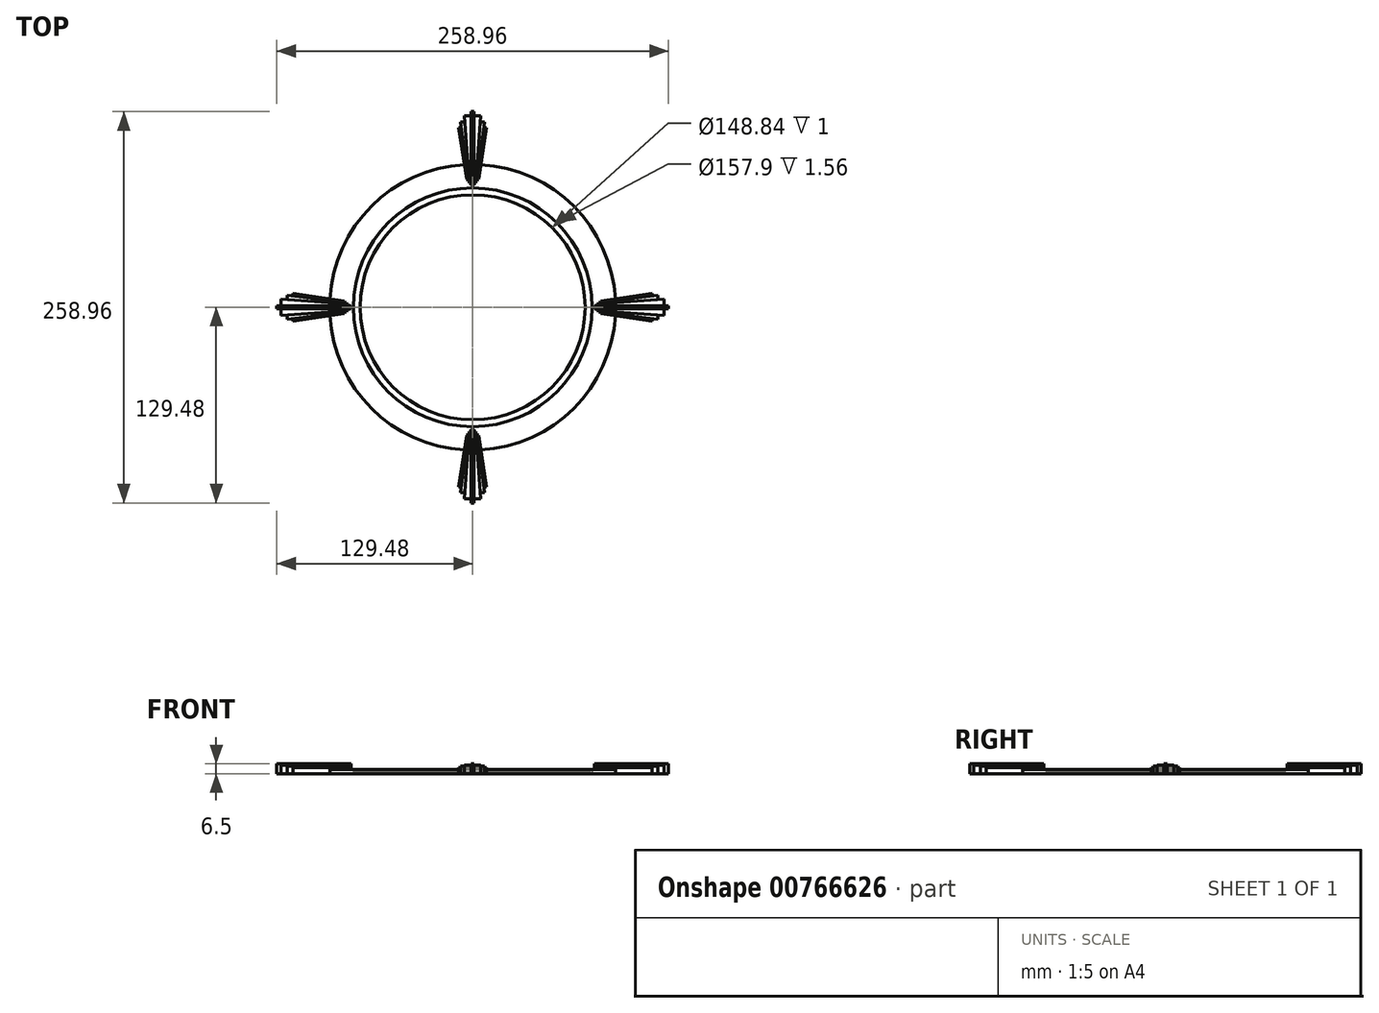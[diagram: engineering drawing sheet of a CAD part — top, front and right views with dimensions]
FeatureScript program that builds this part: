
annotation { "Feature Type Name" : "Feature", "Feature Type Description" : "" }
export const myFeature = defineFeature(function(context is Context, id is Id, definition is map)
    precondition{}
    {
        {
            var Q0;
            Q0=qCreatedBy(makeId("Front.planeOp"),FACE);
            var sketch = newSketch(context, id + "F0", { "sketchPlane" : qUnion([Q0])});
            skLineSegment(sketch, "E0", {"start": v(-74.42, 75) * mm, "end": v(74.45, 75) * mm});
            skLineSegment(sketch, "E1", {"start": v(-74.42, 75) * mm, "end": v(-74.42, 76) * mm});
            skLineSegment(sketch, "E2", {"start": v(-74.42, 76) * mm, "end": v(-78.95, 76) * mm});
            skLineSegment(sketch, "E3", {"start": v(-78.95, 76) * mm, "end": v(-78.95, 77.57) * mm});
            skLineSegment(sketch, "E4", {"start": v(-94.55, 74.8) * mm, "end": v(-74.42, 75) * mm});
            skLineSegment(sketch, "E5", {"start": v(0, 71.55) * mm, "end": v(0, 82.98) * mm});
            skLineSegment(sketch, "E6", {"start": v(-94.55, 74.8) * mm, "end": v(-94.57, 77.47) * mm});
            skLineSegment(sketch, "E7", {"start": v(-78.95, 77.57) * mm, "end": v(-94.57, 77.4) * mm});
            skPoint(sketch, "E7.endSnap0", {"position": v(-94.57, 77.47) * mm});
            skSolve(sketch);
        }
        {
            var Q0;
            Q0=makeQuery(id+"F0.imprint","IMPRINT",FACE,{"disambiguationData":[TD([[makeQuery(id+"F0.imprint","IMPRINT",EDGE,{"derivedFrom":sQuery(id+"F0.wireOp",EDGE,"E1")}),1.0]])]});
            var Q1;
            Q1=sQuery(id+"F0.wireOp",EDGE,"E5");
            revolve(context, id + "F1", {"surfaceOperationType" : NewSurfaceOperationType.NEW, "entities" : qUnion([Q0]), "axis" : qUnion([Q1]), "revolveType" : RevolveType.FULL});
        }
        {
            var Q0;
            Q0=qCreatedBy(makeId("Top.planeOp"),FACE);
            cPlane(context, id + "F2", {"entities" : qUnion([Q0]), "cplaneType" : CPlaneType.OFFSET, "offset" : 75.4 * mm, "width" : 150 * mm, "height" : 150 * mm});
        }
        {
            var Q0;
            Q0=qCreatedBy(id+"F2.planeOp",FACE);
            var sketch = newSketch(context, id + "F3", { "sketchPlane" : qUnion([Q0])});
            skPoint(sketch, "E8.end.orphan", {"position": v(-3.18, 80.53) * mm});
            skLineSegment(sketch, "E9", {"start": v(0, 129.48) * mm, "end": v(-0.97, 129.48) * mm});
            skLineSegment(sketch, "E10", {"start": v(-0.97, 129.48) * mm, "end": v(-0.97, 80.53) * mm});
            skLineSegment(sketch, "E11", {"start": v(-0.97, 80.53) * mm, "end": v(0, 80.53) * mm});
            skLineSegment(sketch, "E12", {"start": v(-0.97, 126.77) * mm, "end": v(-5.43, 126.77) * mm});
            skLineSegment(sketch, "E13", {"start": v(-5.43, 126.77) * mm, "end": v(-2.23, 82.18) * mm});
            skLineSegment(sketch, "E14", {"start": v(-2.23, 82.18) * mm, "end": v(-0.97, 82.18) * mm});
            skLineSegment(sketch, "E15", {"start": v(-5.12, 122.53) * mm, "end": v(-8, 122.53) * mm});
            skLineSegment(sketch, "E16", {"start": v(-8, 122.53) * mm, "end": v(-3.18, 83.42) * mm});
            skLineSegment(sketch, "E17", {"start": v(-3.18, 83.42) * mm, "end": v(-2.32, 83.42) * mm});
            skLineSegment(sketch, "E18", {"start": v(-7.54, 118.72) * mm, "end": v(-9.21, 118.72) * mm});
            skLineSegment(sketch, "E19", {"start": v(-9.21, 118.72) * mm, "end": v(-4, 84.79) * mm});
            skLineSegment(sketch, "E20", {"start": v(-4, 84.79) * mm, "end": v(-3.35, 84.79) * mm});
            skLineSegment(sketch, "E21.MirrorCS", {"start": v(0, 129.48) * mm, "end": v(0.97, 129.48) * mm});
            skLineSegment(sketch, "E22.MirrorCS", {"start": v(0.97, 129.48) * mm, "end": v(0.97, 80.53) * mm});
            skLineSegment(sketch, "E23.MirrorCS", {"start": v(0.97, 126.77) * mm, "end": v(5.43, 126.77) * mm});
            skLineSegment(sketch, "E24.MirrorCS", {"start": v(5.43, 126.77) * mm, "end": v(2.23, 82.18) * mm});
            skLineSegment(sketch, "E25.MirrorCS", {"start": v(5.12, 122.53) * mm, "end": v(8, 122.53) * mm});
            skLineSegment(sketch, "E26.MirrorCS", {"start": v(8, 122.53) * mm, "end": v(3.18, 83.42) * mm});
            skLineSegment(sketch, "E27.MirrorCS", {"start": v(7.54, 118.72) * mm, "end": v(9.21, 118.72) * mm});
            skLineSegment(sketch, "E28.MirrorCS", {"start": v(9.21, 118.72) * mm, "end": v(4, 84.79) * mm});
            skLineSegment(sketch, "E29.MirrorCS", {"start": v(0.97, 80.53) * mm, "end": v(0, 80.53) * mm});
            skLineSegment(sketch, "E30.MirrorCS", {"start": v(2.23, 82.18) * mm, "end": v(0.97, 82.18) * mm});
            skLineSegment(sketch, "E31.MirrorCS", {"start": v(3.18, 83.42) * mm, "end": v(2.32, 83.42) * mm});
            skLineSegment(sketch, "E32.MirrorCS", {"start": v(4, 84.79) * mm, "end": v(3.35, 84.79) * mm});
            skLineSegment(sketch, "E33.MirrorCS", {"start": v(9.21, -118.72) * mm, "end": v(4, -84.79) * mm});
            skLineSegment(sketch, "E34.MirrorCS", {"start": v(8, -122.53) * mm, "end": v(3.18, -83.42) * mm});
            skLineSegment(sketch, "E35.MirrorCS", {"start": v(5.43, -126.77) * mm, "end": v(2.23, -82.18) * mm});
            skLineSegment(sketch, "E36.MirrorCS", {"start": v(0.97, -129.48) * mm, "end": v(0.97, -80.53) * mm});
            skLineSegment(sketch, "E37.MirrorCS", {"start": v(-0.97, -129.48) * mm, "end": v(-0.97, -80.53) * mm});
            skLineSegment(sketch, "E38.MirrorCS", {"start": v(-5.43, -126.77) * mm, "end": v(-2.23, -82.18) * mm});
            skLineSegment(sketch, "E39.MirrorCS", {"start": v(-8, -122.53) * mm, "end": v(-3.18, -83.42) * mm});
            skLineSegment(sketch, "E40.MirrorCS", {"start": v(-9.21, -118.72) * mm, "end": v(-4, -84.79) * mm});
            skLineSegment(sketch, "E41.MirrorCS", {"start": v(-4, -84.79) * mm, "end": v(-3.35, -84.79) * mm});
            skLineSegment(sketch, "E42.MirrorCS", {"start": v(-3.18, -83.42) * mm, "end": v(-2.32, -83.42) * mm});
            skLineSegment(sketch, "E43.MirrorCS", {"start": v(-2.23, -82.18) * mm, "end": v(-0.97, -82.18) * mm});
            skLineSegment(sketch, "E44.MirrorCS", {"start": v(-0.97, -80.53) * mm, "end": v(0, -80.53) * mm});
            skLineSegment(sketch, "E45.MirrorCS", {"start": v(0.97, -80.53) * mm, "end": v(0, -80.53) * mm});
            skLineSegment(sketch, "E46.MirrorCS", {"start": v(2.23, -82.18) * mm, "end": v(0.97, -82.18) * mm});
            skLineSegment(sketch, "E47.MirrorCS", {"start": v(3.18, -83.42) * mm, "end": v(2.32, -83.42) * mm});
            skLineSegment(sketch, "E48.MirrorCS", {"start": v(4, -84.79) * mm, "end": v(3.35, -84.79) * mm});
            skLineSegment(sketch, "E49.MirrorCS", {"start": v(7.54, -118.72) * mm, "end": v(9.21, -118.72) * mm});
            skLineSegment(sketch, "E50.MirrorCS", {"start": v(5.12, -122.53) * mm, "end": v(8, -122.53) * mm});
            skLineSegment(sketch, "E51.MirrorCS", {"start": v(0.97, -126.77) * mm, "end": v(5.43, -126.77) * mm});
            skLineSegment(sketch, "E52.MirrorCS", {"start": v(0, -129.48) * mm, "end": v(0.97, -129.48) * mm});
            skLineSegment(sketch, "E53.MirrorCS", {"start": v(0, -129.48) * mm, "end": v(-0.97, -129.48) * mm});
            skLineSegment(sketch, "E54.MirrorCS", {"start": v(-0.97, -126.77) * mm, "end": v(-5.43, -126.77) * mm});
            skLineSegment(sketch, "E55", {"start": v(0, 0) * mm, "end": v(-80.53, 0) * mm});
            skPoint(sketch, "E56.end.orphan", {"position": v(-80.53, -3.18) * mm});
            skLineSegment(sketch, "E57", {"start": v(-129.48, 0) * mm, "end": v(-129.48, -0.97) * mm});
            skLineSegment(sketch, "E58", {"start": v(-129.48, -0.97) * mm, "end": v(-80.53, -0.97) * mm});
            skLineSegment(sketch, "E59", {"start": v(-80.53, -0.97) * mm, "end": v(-80.53, 0) * mm});
            skLineSegment(sketch, "E60", {"start": v(-126.77, -0.97) * mm, "end": v(-126.77, -5.43) * mm});
            skLineSegment(sketch, "E61", {"start": v(-126.77, -5.43) * mm, "end": v(-82.18, -2.23) * mm});
            skLineSegment(sketch, "E62", {"start": v(-82.18, -2.23) * mm, "end": v(-82.18, -0.97) * mm});
            skLineSegment(sketch, "E63", {"start": v(-122.53, -5.12) * mm, "end": v(-122.53, -8) * mm});
            skLineSegment(sketch, "E64", {"start": v(-122.53, -8) * mm, "end": v(-83.42, -3.18) * mm});
            skLineSegment(sketch, "E65", {"start": v(-83.42, -3.18) * mm, "end": v(-83.42, -2.32) * mm});
            skLineSegment(sketch, "E66", {"start": v(-118.72, -7.54) * mm, "end": v(-118.72, -9.21) * mm});
            skLineSegment(sketch, "E67", {"start": v(-118.72, -9.21) * mm, "end": v(-84.79, -4) * mm});
            skLineSegment(sketch, "E68", {"start": v(-84.79, -4) * mm, "end": v(-84.79, -3.35) * mm});
            skLineSegment(sketch, "E69.MirrorCS", {"start": v(-129.48, 0) * mm, "end": v(-129.48, 0.97) * mm});
            skLineSegment(sketch, "E70.MirrorCS", {"start": v(-129.48, 0.97) * mm, "end": v(-80.53, 0.97) * mm});
            skLineSegment(sketch, "E71.MirrorCS", {"start": v(-126.77, 0.97) * mm, "end": v(-126.77, 5.43) * mm});
            skLineSegment(sketch, "E72.MirrorCS", {"start": v(-126.77, 5.43) * mm, "end": v(-82.18, 2.23) * mm});
            skLineSegment(sketch, "E73.MirrorCS", {"start": v(-122.53, 5.12) * mm, "end": v(-122.53, 8) * mm});
            skLineSegment(sketch, "E74.MirrorCS", {"start": v(-122.53, 8) * mm, "end": v(-83.42, 3.18) * mm});
            skLineSegment(sketch, "E75.MirrorCS", {"start": v(-118.72, 7.54) * mm, "end": v(-118.72, 9.21) * mm});
            skLineSegment(sketch, "E76.MirrorCS", {"start": v(-118.72, 9.21) * mm, "end": v(-84.79, 4) * mm});
            skLineSegment(sketch, "E77.MirrorCS", {"start": v(-80.53, 0.97) * mm, "end": v(-80.53, 0) * mm});
            skLineSegment(sketch, "E78.MirrorCS", {"start": v(-82.18, 2.23) * mm, "end": v(-82.18, 0.97) * mm});
            skLineSegment(sketch, "E79.MirrorCS", {"start": v(-83.42, 3.18) * mm, "end": v(-83.42, 2.32) * mm});
            skLineSegment(sketch, "E80.MirrorCS", {"start": v(-84.79, 4) * mm, "end": v(-84.79, 3.35) * mm});
            skLineSegment(sketch, "E81.MirrorCS", {"start": v(129.48, -0.97) * mm, "end": v(80.53, -0.97) * mm});
            skLineSegment(sketch, "E82.MirrorCS", {"start": v(129.48, 0.97) * mm, "end": v(80.53, 0.97) * mm});
            skLineSegment(sketch, "E83.MirrorCS", {"start": v(126.77, 5.43) * mm, "end": v(82.18, 2.23) * mm});
            skLineSegment(sketch, "E84.MirrorCS", {"start": v(122.53, 8) * mm, "end": v(83.42, 3.18) * mm});
            skLineSegment(sketch, "E85.MirrorCS", {"start": v(118.72, 9.21) * mm, "end": v(84.79, 4) * mm});
            skLineSegment(sketch, "E86.MirrorCS", {"start": v(118.72, -9.21) * mm, "end": v(84.79, -4) * mm});
            skLineSegment(sketch, "E87.MirrorCS", {"start": v(122.53, -8) * mm, "end": v(83.42, -3.18) * mm});
            skLineSegment(sketch, "E88.MirrorCS", {"start": v(126.77, -5.43) * mm, "end": v(82.18, -2.23) * mm});
            skLineSegment(sketch, "E89.MirrorCS", {"start": v(80.53, -0.97) * mm, "end": v(80.53, 0) * mm});
            skLineSegment(sketch, "E90.MirrorCS", {"start": v(80.53, 0.97) * mm, "end": v(80.53, 0) * mm});
            skLineSegment(sketch, "E91.MirrorCS", {"start": v(82.18, 2.23) * mm, "end": v(82.18, 0.97) * mm});
            skLineSegment(sketch, "E92.MirrorCS", {"start": v(83.42, 3.18) * mm, "end": v(83.42, 2.32) * mm});
            skLineSegment(sketch, "E93.MirrorCS", {"start": v(84.79, 4) * mm, "end": v(84.79, 3.35) * mm});
            skLineSegment(sketch, "E94.MirrorCS", {"start": v(82.18, -2.23) * mm, "end": v(82.18, -0.97) * mm});
            skLineSegment(sketch, "E95.MirrorCS", {"start": v(83.42, -3.18) * mm, "end": v(83.42, -2.32) * mm});
            skLineSegment(sketch, "E96.MirrorCS", {"start": v(84.79, -4) * mm, "end": v(84.79, -3.35) * mm});
            skLineSegment(sketch, "E97.MirrorCS", {"start": v(118.72, 7.54) * mm, "end": v(118.72, 9.21) * mm});
            skLineSegment(sketch, "E98.MirrorCS", {"start": v(122.53, 5.12) * mm, "end": v(122.53, 8) * mm});
            skLineSegment(sketch, "E99.MirrorCS", {"start": v(126.77, 0.97) * mm, "end": v(126.77, 5.43) * mm});
            skLineSegment(sketch, "E100.MirrorCS", {"start": v(129.48, 0) * mm, "end": v(129.48, 0.97) * mm});
            skLineSegment(sketch, "E101.MirrorCS", {"start": v(129.48, 0) * mm, "end": v(129.48, -0.97) * mm});
            skLineSegment(sketch, "E102.MirrorCS", {"start": v(126.77, -0.97) * mm, "end": v(126.77, -5.43) * mm});
            skLineSegment(sketch, "E103.MirrorCS", {"start": v(122.53, -5.12) * mm, "end": v(122.53, -8) * mm});
            skLineSegment(sketch, "E104.MirrorCS", {"start": v(118.72, -7.54) * mm, "end": v(118.72, -9.21) * mm});
            skLineSegment(sketch, "E105.MirrorCS", {"start": v(-7.54, -118.72) * mm, "end": v(-9.21, -118.72) * mm});
            skLineSegment(sketch, "E106.MirrorCS", {"start": v(-5.12, -122.53) * mm, "end": v(-8, -122.53) * mm});
            skSolve(sketch);
        }
        {
            var Q0;
            {var subQ4=sQuery(id+"F3.wireOp",EDGE,"E57");Q0=makeQuery(id+"F3.imprint","IMPRINT",FACE,{"disambiguationData":[TD([[makeQuery(id+"F3.imprint","IMPRINT",EDGE,{"derivedFrom":subQ4}),1.0]])]});}
            extrude(context, id + "F4", {"entities" : qUnion([Q0]), "operationType" : NewBodyOperationType.ADD, "depth" : 5.9 * mm, "offsetDistance" : 25 * mm});
        }
        {
            var Q0;
            {var subQ4=sQuery(id+"F3.wireOp",EDGE,"E9");Q0=makeQuery(id+"F3.imprint","IMPRINT",FACE,{"disambiguationData":[TD([[makeQuery(id+"F3.imprint","IMPRINT",EDGE,{"derivedFrom":subQ4}),1.0]])]});}
            extrude(context, id + "F5", {"entities" : qUnion([Q0]), "operationType" : NewBodyOperationType.ADD, "depth" : 5.9 * mm, "offsetDistance" : 25 * mm});
        }
        {
            var Q0;
            {var subQ9=sQuery(id+"F3.wireOp",EDGE,"E89.MirrorCS");Q0=makeQuery(id+"F3.imprint","IMPRINT",FACE,{"disambiguationData":[TD([[makeQuery(id+"F3.imprint","IMPRINT",EDGE,{"derivedFrom":subQ9}),-1.0]])]});}
            extrude(context, id + "F6", {"entities" : qUnion([Q0]), "operationType" : NewBodyOperationType.ADD, "depth" : 5.9 * mm, "offsetDistance" : 25 * mm});
        }
        {
            var Q0;
            {var subQ9=sQuery(id+"F3.wireOp",EDGE,"E44.MirrorCS");Q0=makeQuery(id+"F3.imprint","IMPRINT",FACE,{"disambiguationData":[TD([[makeQuery(id+"F3.imprint","IMPRINT",EDGE,{"derivedFrom":subQ9}),-1.0]])]});}
            extrude(context, id + "F7", {"entities" : qUnion([Q0]), "operationType" : NewBodyOperationType.ADD, "depth" : 5.9 * mm, "offsetDistance" : 25 * mm});
        }
        {
            var Q0;
            {var subQ0=sQuery(id+"F3.wireOp",EDGE,"E43.MirrorCS");Q0=makeQuery(id+"F3.imprint","IMPRINT",FACE,{"disambiguationData":[TD([[makeQuery(id+"F3.imprint","IMPRINT",EDGE,{"derivedFrom":subQ0}),-1.0]])]});}
            extrude(context, id + "F8", {"entities" : qUnion([Q0]), "operationType" : NewBodyOperationType.ADD, "depth" : 5.1 * mm, "offsetDistance" : 25 * mm});
        }
        {
            var Q0;
            {var subQ0=sQuery(id+"F3.wireOp",EDGE,"E46.MirrorCS");Q0=makeQuery(id+"F3.imprint","IMPRINT",FACE,{"disambiguationData":[TD([[makeQuery(id+"F3.imprint","IMPRINT",EDGE,{"derivedFrom":subQ0}),1.0]])]});}
            extrude(context, id + "F9", {"entities" : qUnion([Q0]), "operationType" : NewBodyOperationType.ADD, "depth" : 5.1 * mm, "offsetDistance" : 25 * mm});
        }
        {
            var Q0;
            {var subQ3=sQuery(id+"F3.wireOp",EDGE,"E23.MirrorCS");Q0=makeQuery(id+"F3.imprint","IMPRINT",FACE,{"disambiguationData":[TD([[makeQuery(id+"F3.imprint","IMPRINT",EDGE,{"derivedFrom":subQ3}),-1.0]])]});}
            extrude(context, id + "F10", {"entities" : qUnion([Q0]), "operationType" : NewBodyOperationType.ADD, "depth" : 5.1 * mm, "offsetDistance" : 25 * mm});
        }
        {
            var Q0;
            {var subQ1=sQuery(id+"F3.wireOp",EDGE,"E12");Q0=makeQuery(id+"F3.imprint","IMPRINT",FACE,{"disambiguationData":[TD([[makeQuery(id+"F3.imprint","IMPRINT",EDGE,{"derivedFrom":subQ1}),1.0]])]});}
            extrude(context, id + "F11", {"entities" : qUnion([Q0]), "operationType" : NewBodyOperationType.ADD, "depth" : 5.1 * mm, "offsetDistance" : 25 * mm});
        }
        {
            var Q0;
            {var subQ3=sQuery(id+"F3.wireOp",EDGE,"E71.MirrorCS");Q0=makeQuery(id+"F3.imprint","IMPRINT",FACE,{"disambiguationData":[TD([[makeQuery(id+"F3.imprint","IMPRINT",EDGE,{"derivedFrom":subQ3}),-1.0]])]});}
            extrude(context, id + "F12", {"entities" : qUnion([Q0]), "operationType" : NewBodyOperationType.ADD, "depth" : 5.1 * mm, "offsetDistance" : 25 * mm});
        }
        {
            var Q0;
            {var subQ1=sQuery(id+"F3.wireOp",EDGE,"E60");Q0=makeQuery(id+"F3.imprint","IMPRINT",FACE,{"disambiguationData":[TD([[makeQuery(id+"F3.imprint","IMPRINT",EDGE,{"derivedFrom":subQ1}),1.0]])]});}
            extrude(context, id + "F13", {"entities" : qUnion([Q0]), "operationType" : NewBodyOperationType.ADD, "depth" : 5.1 * mm, "offsetDistance" : 25 * mm});
        }
        {
            var Q0;
            {var subQ0=sQuery(id+"F3.wireOp",EDGE,"E91.MirrorCS");Q0=makeQuery(id+"F3.imprint","IMPRINT",FACE,{"disambiguationData":[TD([[makeQuery(id+"F3.imprint","IMPRINT",EDGE,{"derivedFrom":subQ0}),1.0]])]});}
            extrude(context, id + "F14", {"entities" : qUnion([Q0]), "operationType" : NewBodyOperationType.ADD, "depth" : 5.1 * mm, "offsetDistance" : 25 * mm});
        }
        {
            var Q0;
            {var subQ0=sQuery(id+"F3.wireOp",EDGE,"E94.MirrorCS");Q0=makeQuery(id+"F3.imprint","IMPRINT",FACE,{"disambiguationData":[TD([[makeQuery(id+"F3.imprint","IMPRINT",EDGE,{"derivedFrom":subQ0}),-1.0]])]});}
            extrude(context, id + "F15", {"entities" : qUnion([Q0]), "operationType" : NewBodyOperationType.ADD, "depth" : 5.1 * mm, "offsetDistance" : 25 * mm});
        }
        {
            var Q0;
            {var subQ1=sQuery(id+"F3.wireOp",EDGE,"E15");Q0=makeQuery(id+"F3.imprint","IMPRINT",FACE,{"disambiguationData":[TD([[makeQuery(id+"F3.imprint","IMPRINT",EDGE,{"derivedFrom":subQ1}),1.0]])]});}
            extrude(context, id + "F16", {"entities" : qUnion([Q0]), "operationType" : NewBodyOperationType.ADD, "depth" : 4.2 * mm, "offsetDistance" : 25 * mm});
        }
        {
            var Q0;
            {var subQ3=sQuery(id+"F3.wireOp",EDGE,"E25.MirrorCS");Q0=makeQuery(id+"F3.imprint","IMPRINT",FACE,{"disambiguationData":[TD([[makeQuery(id+"F3.imprint","IMPRINT",EDGE,{"derivedFrom":subQ3}),-1.0]])]});}
            extrude(context, id + "F17", {"entities" : qUnion([Q0]), "operationType" : NewBodyOperationType.ADD, "depth" : 4.2 * mm, "offsetDistance" : 25 * mm});
        }
        {
            var Q0;
            {var subQ1=sQuery(id+"F3.wireOp",EDGE,"E63");Q0=makeQuery(id+"F3.imprint","IMPRINT",FACE,{"disambiguationData":[TD([[makeQuery(id+"F3.imprint","IMPRINT",EDGE,{"derivedFrom":subQ1}),1.0]])]});}
            extrude(context, id + "F18", {"entities" : qUnion([Q0]), "operationType" : NewBodyOperationType.ADD, "depth" : 4.2 * mm, "offsetDistance" : 25 * mm});
        }
        {
            var Q0;
            {var subQ3=sQuery(id+"F3.wireOp",EDGE,"E73.MirrorCS");Q0=makeQuery(id+"F3.imprint","IMPRINT",FACE,{"disambiguationData":[TD([[makeQuery(id+"F3.imprint","IMPRINT",EDGE,{"derivedFrom":subQ3}),-1.0]])]});}
            extrude(context, id + "F19", {"entities" : qUnion([Q0]), "operationType" : NewBodyOperationType.ADD, "depth" : 4.2 * mm, "offsetDistance" : 25 * mm});
        }
        {
            var Q0;
            {var subQ0=sQuery(id+"F3.wireOp",EDGE,"E95.MirrorCS");Q0=makeQuery(id+"F3.imprint","IMPRINT",FACE,{"disambiguationData":[TD([[makeQuery(id+"F3.imprint","IMPRINT",EDGE,{"derivedFrom":subQ0}),-1.0]])]});}
            extrude(context, id + "F20", {"entities" : qUnion([Q0]), "operationType" : NewBodyOperationType.ADD, "depth" : 4.2 * mm, "offsetDistance" : 25 * mm});
        }
        {
            var Q0;
            {var subQ0=sQuery(id+"F3.wireOp",EDGE,"E92.MirrorCS");Q0=makeQuery(id+"F3.imprint","IMPRINT",FACE,{"disambiguationData":[TD([[makeQuery(id+"F3.imprint","IMPRINT",EDGE,{"derivedFrom":subQ0}),1.0]])]});}
            extrude(context, id + "F21", {"entities" : qUnion([Q0]), "operationType" : NewBodyOperationType.ADD, "depth" : 4.2 * mm, "offsetDistance" : 25 * mm});
        }
        {
            var Q0;
            {var subQ0=sQuery(id+"F3.wireOp",EDGE,"E47.MirrorCS");Q0=makeQuery(id+"F3.imprint","IMPRINT",FACE,{"disambiguationData":[TD([[makeQuery(id+"F3.imprint","IMPRINT",EDGE,{"derivedFrom":subQ0}),1.0]])]});}
            extrude(context, id + "F22", {"entities" : qUnion([Q0]), "operationType" : NewBodyOperationType.ADD, "depth" : 4.2 * mm, "offsetDistance" : 25 * mm});
        }
        {
            var Q0;
            {var subQ0=sQuery(id+"F3.wireOp",EDGE,"E42.MirrorCS");Q0=makeQuery(id+"F3.imprint","IMPRINT",FACE,{"disambiguationData":[TD([[makeQuery(id+"F3.imprint","IMPRINT",EDGE,{"derivedFrom":subQ0}),-1.0]])]});}
            extrude(context, id + "F23", {"entities" : qUnion([Q0]), "operationType" : NewBodyOperationType.ADD, "depth" : 4.2 * mm, "offsetDistance" : 25 * mm});
        }
        {
            var Q0;
            Q0=makeQuery(id+"F3.imprint","IMPRINT",FACE,{"disambiguationData":[TD([[makeQuery(id+"F3.imprint","IMPRINT",EDGE,{"derivedFrom":sQuery(id+"F3.wireOp",EDGE,"E33.MirrorCS")}),1.0]])]});
            extrude(context, id + "F24", {"entities" : qUnion([Q0]), "operationType" : NewBodyOperationType.ADD, "depth" : 3.3 * mm, "offsetDistance" : 25 * mm});
        }
        {
            var Q0;
            Q0=makeQuery(id+"F3.imprint","IMPRINT",FACE,{"disambiguationData":[TD([[makeQuery(id+"F3.imprint","IMPRINT",EDGE,{"derivedFrom":sQuery(id+"F3.wireOp",EDGE,"E40.MirrorCS")}),-1.0]])]});
            extrude(context, id + "F25", {"entities" : qUnion([Q0]), "operationType" : NewBodyOperationType.ADD, "depth" : 3.3 * mm, "offsetDistance" : 25 * mm});
        }
        {
            var Q0;
            {var subQ0=sQuery(id+"F3.wireOp",EDGE,"E18");Q0=makeQuery(id+"F3.imprint","IMPRINT",FACE,{"disambiguationData":[TD([[makeQuery(id+"F3.imprint","IMPRINT",EDGE,{"derivedFrom":subQ0}),1.0]])]});}
            extrude(context, id + "F26", {"entities" : qUnion([Q0]), "operationType" : NewBodyOperationType.ADD, "depth" : 3.3 * mm, "offsetDistance" : 25 * mm});
        }
        {
            var Q0;
            {var subQ0=sQuery(id+"F3.wireOp",EDGE,"E27.MirrorCS");Q0=makeQuery(id+"F3.imprint","IMPRINT",FACE,{"disambiguationData":[TD([[makeQuery(id+"F3.imprint","IMPRINT",EDGE,{"derivedFrom":subQ0}),-1.0]])]});}
            extrude(context, id + "F27", {"entities" : qUnion([Q0]), "operationType" : NewBodyOperationType.ADD, "depth" : 3.3 * mm, "offsetDistance" : 25 * mm});
        }
        {
            var Q0;
            {var subQ0=sQuery(id+"F3.wireOp",EDGE,"E75.MirrorCS");Q0=makeQuery(id+"F3.imprint","IMPRINT",FACE,{"disambiguationData":[TD([[makeQuery(id+"F3.imprint","IMPRINT",EDGE,{"derivedFrom":subQ0}),-1.0]])]});}
            extrude(context, id + "F28", {"entities" : qUnion([Q0]), "operationType" : NewBodyOperationType.ADD, "depth" : 3.3 * mm, "offsetDistance" : 25 * mm});
        }
        {
            var Q0;
            {var subQ0=sQuery(id+"F3.wireOp",EDGE,"E66");Q0=makeQuery(id+"F3.imprint","IMPRINT",FACE,{"disambiguationData":[TD([[makeQuery(id+"F3.imprint","IMPRINT",EDGE,{"derivedFrom":subQ0}),1.0]])]});}
            extrude(context, id + "F29", {"entities" : qUnion([Q0]), "operationType" : NewBodyOperationType.ADD, "depth" : 3.3 * mm, "offsetDistance" : 25 * mm});
        }
        {
            var Q0;
            Q0=makeQuery(id+"F3.imprint","IMPRINT",FACE,{"disambiguationData":[TD([[makeQuery(id+"F3.imprint","IMPRINT",EDGE,{"derivedFrom":sQuery(id+"F3.wireOp",EDGE,"E86.MirrorCS")}),-1.0]])]});
            extrude(context, id + "F30", {"entities" : qUnion([Q0]), "operationType" : NewBodyOperationType.ADD, "depth" : 3.3 * mm, "offsetDistance" : 25 * mm});
        }
        {
            var Q0;
            Q0=makeQuery(id+"F3.imprint","IMPRINT",FACE,{"disambiguationData":[TD([[makeQuery(id+"F3.imprint","IMPRINT",EDGE,{"derivedFrom":sQuery(id+"F3.wireOp",EDGE,"E85.MirrorCS")}),1.0]])]});
            extrude(context, id + "F31", {"entities" : qUnion([Q0]), "operationType" : NewBodyOperationType.ADD, "depth" : 3.3 * mm, "offsetDistance" : 25 * mm});
        }
        {
            var Q0;
            {var subQ0=sQuery(id+"F3.wireOp",EDGE,"E64");var subQ1=sQuery(id+"F3.wireOp",EDGE,"E74.MirrorCS");var subQ2=sQuery(id+"F3.wireOp",EDGE,"E72.MirrorCS");var subQ3=sQuery(id+"F3.wireOp",EDGE,"E61");var subQ4=sQuery(id+"F3.wireOp",EDGE,"E58");var subQ5=sQuery(id+"F3.wireOp",EDGE,"E70.MirrorCS");Q0=makeQuery(id+"F29.boolean.opBoolean","MERGE",FACE,{"derivedFrom":[makeQuery(id+"F28.boolean.opBoolean","MERGE",FACE,{"derivedFrom":[makeQuery(id+"F19.boolean.opBoolean","MERGE",FACE,{"derivedFrom":[makeQuery(id+"F18.boolean.opBoolean","MERGE",FACE,{"derivedFrom":[makeQuery(id+"F13.boolean.opBoolean","MERGE",FACE,{"derivedFrom":[makeQuery(id+"F12.boolean.opBoolean","MERGE",FACE,{"derivedFrom":[makeQuery(id+"F4.opExtrude","CAP_FACE",FACE,{"disambiguationData":[OSD([sQuery(id+"F3.wireOp",EDGE,"E57"),subQ4,sQuery(id+"F3.wireOp",EDGE,"E59"),sQuery(id+"F3.wireOp",EDGE,"E69.MirrorCS"),subQ5,sQuery(id+"F3.wireOp",EDGE,"E77.MirrorCS")])],"isStart":true}),makeQuery(id+"F12.opExtrude","CAP_FACE",FACE,{"disambiguationData":[OSD([subQ5,sQuery(id+"F3.wireOp",EDGE,"E71.MirrorCS"),subQ2,sQuery(id+"F3.wireOp",EDGE,"E78.MirrorCS")])],"isStart":true})]}),makeQuery(id+"F13.opExtrude","CAP_FACE",FACE,{"disambiguationData":[OSD([subQ4,sQuery(id+"F3.wireOp",EDGE,"E60"),subQ3,sQuery(id+"F3.wireOp",EDGE,"E62")])],"isStart":true})]}),makeQuery(id+"F18.opExtrude","CAP_FACE",FACE,{"disambiguationData":[OSD([subQ3,sQuery(id+"F3.wireOp",EDGE,"E63"),subQ0,sQuery(id+"F3.wireOp",EDGE,"E65")])],"isStart":true})]}),makeQuery(id+"F19.opExtrude","CAP_FACE",FACE,{"disambiguationData":[OSD([subQ2,sQuery(id+"F3.wireOp",EDGE,"E73.MirrorCS"),subQ1,sQuery(id+"F3.wireOp",EDGE,"E79.MirrorCS")])],"isStart":true})]}),makeQuery(id+"F28.opExtrude","CAP_FACE",FACE,{"disambiguationData":[OSD([subQ1,sQuery(id+"F3.wireOp",EDGE,"E75.MirrorCS"),sQuery(id+"F3.wireOp",EDGE,"E76.MirrorCS"),sQuery(id+"F3.wireOp",EDGE,"E80.MirrorCS")])],"isStart":true})]}),makeQuery(id+"F29.opExtrude","CAP_FACE",FACE,{"disambiguationData":[OSD([subQ0,sQuery(id+"F3.wireOp",EDGE,"E66"),sQuery(id+"F3.wireOp",EDGE,"E67"),sQuery(id+"F3.wireOp",EDGE,"E68")])],"isStart":true})]});}
            extrude(context, id + "F32", {"entities" : qUnion([Q0]), "operationType" : NewBodyOperationType.ADD, "depth" : 0.6 * mm, "offsetDistance" : 25 * mm});
        }
        {
            var Q0;
            {var subQ0=sQuery(id+"F3.wireOp",EDGE,"E26.MirrorCS");var subQ1=sQuery(id+"F3.wireOp",EDGE,"E16");var subQ2=sQuery(id+"F3.wireOp",EDGE,"E24.MirrorCS");var subQ3=sQuery(id+"F3.wireOp",EDGE,"E13");var subQ4=sQuery(id+"F3.wireOp",EDGE,"E10");var subQ5=sQuery(id+"F3.wireOp",EDGE,"E22.MirrorCS");Q0=makeQuery(id+"F27.boolean.opBoolean","MERGE",FACE,{"derivedFrom":[makeQuery(id+"F26.boolean.opBoolean","MERGE",FACE,{"derivedFrom":[makeQuery(id+"F17.boolean.opBoolean","MERGE",FACE,{"derivedFrom":[makeQuery(id+"F16.boolean.opBoolean","MERGE",FACE,{"derivedFrom":[makeQuery(id+"F11.boolean.opBoolean","MERGE",FACE,{"derivedFrom":[makeQuery(id+"F10.boolean.opBoolean","MERGE",FACE,{"derivedFrom":[makeQuery(id+"F5.opExtrude","CAP_FACE",FACE,{"disambiguationData":[OSD([sQuery(id+"F3.wireOp",EDGE,"E9"),subQ4,sQuery(id+"F3.wireOp",EDGE,"E11"),sQuery(id+"F3.wireOp",EDGE,"E21.MirrorCS"),subQ5,sQuery(id+"F3.wireOp",EDGE,"E29.MirrorCS")])],"isStart":true}),makeQuery(id+"F10.opExtrude","CAP_FACE",FACE,{"disambiguationData":[OSD([subQ5,sQuery(id+"F3.wireOp",EDGE,"E23.MirrorCS"),subQ2,sQuery(id+"F3.wireOp",EDGE,"E30.MirrorCS")])],"isStart":true})]}),makeQuery(id+"F11.opExtrude","CAP_FACE",FACE,{"disambiguationData":[OSD([subQ4,sQuery(id+"F3.wireOp",EDGE,"E12"),subQ3,sQuery(id+"F3.wireOp",EDGE,"E14")])],"isStart":true})]}),makeQuery(id+"F16.opExtrude","CAP_FACE",FACE,{"disambiguationData":[OSD([subQ3,sQuery(id+"F3.wireOp",EDGE,"E15"),subQ1,sQuery(id+"F3.wireOp",EDGE,"E17")])],"isStart":true})]}),makeQuery(id+"F17.opExtrude","CAP_FACE",FACE,{"disambiguationData":[OSD([subQ2,sQuery(id+"F3.wireOp",EDGE,"E25.MirrorCS"),subQ0,sQuery(id+"F3.wireOp",EDGE,"E31.MirrorCS")])],"isStart":true})]}),makeQuery(id+"F26.opExtrude","CAP_FACE",FACE,{"disambiguationData":[OSD([subQ1,sQuery(id+"F3.wireOp",EDGE,"E18"),sQuery(id+"F3.wireOp",EDGE,"E19"),sQuery(id+"F3.wireOp",EDGE,"E20")])],"isStart":true})]}),makeQuery(id+"F27.opExtrude","CAP_FACE",FACE,{"disambiguationData":[OSD([subQ0,sQuery(id+"F3.wireOp",EDGE,"E27.MirrorCS"),sQuery(id+"F3.wireOp",EDGE,"E28.MirrorCS"),sQuery(id+"F3.wireOp",EDGE,"E32.MirrorCS")])],"isStart":true})]});}
            extrude(context, id + "F33", {"entities" : qUnion([Q0]), "operationType" : NewBodyOperationType.ADD, "depth" : 0.6 * mm, "offsetDistance" : 25 * mm});
        }
        {
            var Q0;
            {var subQ0=sQuery(id+"F3.wireOp",EDGE,"E84.MirrorCS");var subQ1=sQuery(id+"F3.wireOp",EDGE,"E87.MirrorCS");var subQ2=sQuery(id+"F3.wireOp",EDGE,"E83.MirrorCS");var subQ3=sQuery(id+"F3.wireOp",EDGE,"E88.MirrorCS");var subQ4=sQuery(id+"F3.wireOp",EDGE,"E81.MirrorCS");var subQ5=sQuery(id+"F3.wireOp",EDGE,"E82.MirrorCS");Q0=makeQuery(id+"F31.boolean.opBoolean","MERGE",FACE,{"derivedFrom":[makeQuery(id+"F30.boolean.opBoolean","MERGE",FACE,{"derivedFrom":[makeQuery(id+"F21.boolean.opBoolean","MERGE",FACE,{"derivedFrom":[makeQuery(id+"F20.boolean.opBoolean","MERGE",FACE,{"derivedFrom":[makeQuery(id+"F15.boolean.opBoolean","MERGE",FACE,{"derivedFrom":[makeQuery(id+"F14.boolean.opBoolean","MERGE",FACE,{"derivedFrom":[makeQuery(id+"F6.opExtrude","CAP_FACE",FACE,{"disambiguationData":[OSD([subQ5,subQ4,sQuery(id+"F3.wireOp",EDGE,"E89.MirrorCS"),sQuery(id+"F3.wireOp",EDGE,"E90.MirrorCS"),sQuery(id+"F3.wireOp",EDGE,"E100.MirrorCS"),sQuery(id+"F3.wireOp",EDGE,"E101.MirrorCS")])],"isStart":true}),makeQuery(id+"F14.opExtrude","CAP_FACE",FACE,{"disambiguationData":[OSD([subQ5,subQ2,sQuery(id+"F3.wireOp",EDGE,"E91.MirrorCS"),sQuery(id+"F3.wireOp",EDGE,"E99.MirrorCS")])],"isStart":true})]}),makeQuery(id+"F15.opExtrude","CAP_FACE",FACE,{"disambiguationData":[OSD([subQ3,subQ4,sQuery(id+"F3.wireOp",EDGE,"E94.MirrorCS"),sQuery(id+"F3.wireOp",EDGE,"E102.MirrorCS")])],"isStart":true})]}),makeQuery(id+"F20.opExtrude","CAP_FACE",FACE,{"disambiguationData":[OSD([subQ1,subQ3,sQuery(id+"F3.wireOp",EDGE,"E95.MirrorCS"),sQuery(id+"F3.wireOp",EDGE,"E103.MirrorCS")])],"isStart":true})]}),makeQuery(id+"F21.opExtrude","CAP_FACE",FACE,{"disambiguationData":[OSD([subQ2,subQ0,sQuery(id+"F3.wireOp",EDGE,"E92.MirrorCS"),sQuery(id+"F3.wireOp",EDGE,"E98.MirrorCS")])],"isStart":true})]}),makeQuery(id+"F30.opExtrude","CAP_FACE",FACE,{"disambiguationData":[OSD([sQuery(id+"F3.wireOp",EDGE,"E86.MirrorCS"),subQ1,sQuery(id+"F3.wireOp",EDGE,"E96.MirrorCS"),sQuery(id+"F3.wireOp",EDGE,"E104.MirrorCS")])],"isStart":true})]}),makeQuery(id+"F31.opExtrude","CAP_FACE",FACE,{"disambiguationData":[OSD([subQ0,sQuery(id+"F3.wireOp",EDGE,"E85.MirrorCS"),sQuery(id+"F3.wireOp",EDGE,"E93.MirrorCS"),sQuery(id+"F3.wireOp",EDGE,"E97.MirrorCS")])],"isStart":true})]});}
            extrude(context, id + "F34", {"entities" : qUnion([Q0]), "operationType" : NewBodyOperationType.ADD, "depth" : 0.6 * mm, "offsetDistance" : 25 * mm});
        }
        {
            var Q0;
            {var subQ0=sQuery(id+"F3.wireOp",EDGE,"E39.MirrorCS");var subQ1=sQuery(id+"F3.wireOp",EDGE,"E34.MirrorCS");var subQ2=sQuery(id+"F3.wireOp",EDGE,"E38.MirrorCS");var subQ3=sQuery(id+"F3.wireOp",EDGE,"E35.MirrorCS");var subQ4=sQuery(id+"F3.wireOp",EDGE,"E36.MirrorCS");var subQ5=sQuery(id+"F3.wireOp",EDGE,"E37.MirrorCS");Q0=makeQuery(id+"F25.boolean.opBoolean","MERGE",FACE,{"derivedFrom":[makeQuery(id+"F24.boolean.opBoolean","MERGE",FACE,{"derivedFrom":[makeQuery(id+"F23.boolean.opBoolean","MERGE",FACE,{"derivedFrom":[makeQuery(id+"F22.boolean.opBoolean","MERGE",FACE,{"derivedFrom":[makeQuery(id+"F9.boolean.opBoolean","MERGE",FACE,{"derivedFrom":[makeQuery(id+"F8.boolean.opBoolean","MERGE",FACE,{"derivedFrom":[makeQuery(id+"F7.opExtrude","CAP_FACE",FACE,{"disambiguationData":[OSD([subQ4,subQ5,sQuery(id+"F3.wireOp",EDGE,"E44.MirrorCS"),sQuery(id+"F3.wireOp",EDGE,"E45.MirrorCS"),sQuery(id+"F3.wireOp",EDGE,"E52.MirrorCS"),sQuery(id+"F3.wireOp",EDGE,"E53.MirrorCS")])],"isStart":true}),makeQuery(id+"F8.opExtrude","CAP_FACE",FACE,{"disambiguationData":[OSD([subQ5,subQ2,sQuery(id+"F3.wireOp",EDGE,"E43.MirrorCS"),sQuery(id+"F3.wireOp",EDGE,"E54.MirrorCS")])],"isStart":true})]}),makeQuery(id+"F9.opExtrude","CAP_FACE",FACE,{"disambiguationData":[OSD([subQ3,subQ4,sQuery(id+"F3.wireOp",EDGE,"E46.MirrorCS"),sQuery(id+"F3.wireOp",EDGE,"E51.MirrorCS")])],"isStart":true})]}),makeQuery(id+"F22.opExtrude","CAP_FACE",FACE,{"disambiguationData":[OSD([subQ1,subQ3,sQuery(id+"F3.wireOp",EDGE,"E47.MirrorCS"),sQuery(id+"F3.wireOp",EDGE,"E50.MirrorCS")])],"isStart":true})]}),makeQuery(id+"F23.opExtrude","CAP_FACE",FACE,{"disambiguationData":[OSD([subQ2,subQ0,sQuery(id+"F3.wireOp",EDGE,"E42.MirrorCS"),sQuery(id+"F3.wireOp",EDGE,"E106.MirrorCS")])],"isStart":true})]}),makeQuery(id+"F24.opExtrude","CAP_FACE",FACE,{"disambiguationData":[OSD([sQuery(id+"F3.wireOp",EDGE,"E33.MirrorCS"),subQ1,sQuery(id+"F3.wireOp",EDGE,"E48.MirrorCS"),sQuery(id+"F3.wireOp",EDGE,"E49.MirrorCS")])],"isStart":true})]}),makeQuery(id+"F25.opExtrude","CAP_FACE",FACE,{"disambiguationData":[OSD([subQ0,sQuery(id+"F3.wireOp",EDGE,"E40.MirrorCS"),sQuery(id+"F3.wireOp",EDGE,"E41.MirrorCS"),sQuery(id+"F3.wireOp",EDGE,"E105.MirrorCS")])],"isStart":true})]});}
            extrude(context, id + "F35", {"entities" : qUnion([Q0]), "operationType" : NewBodyOperationType.ADD, "depth" : 0.6 * mm, "offsetDistance" : 25 * mm});
        }
    });
